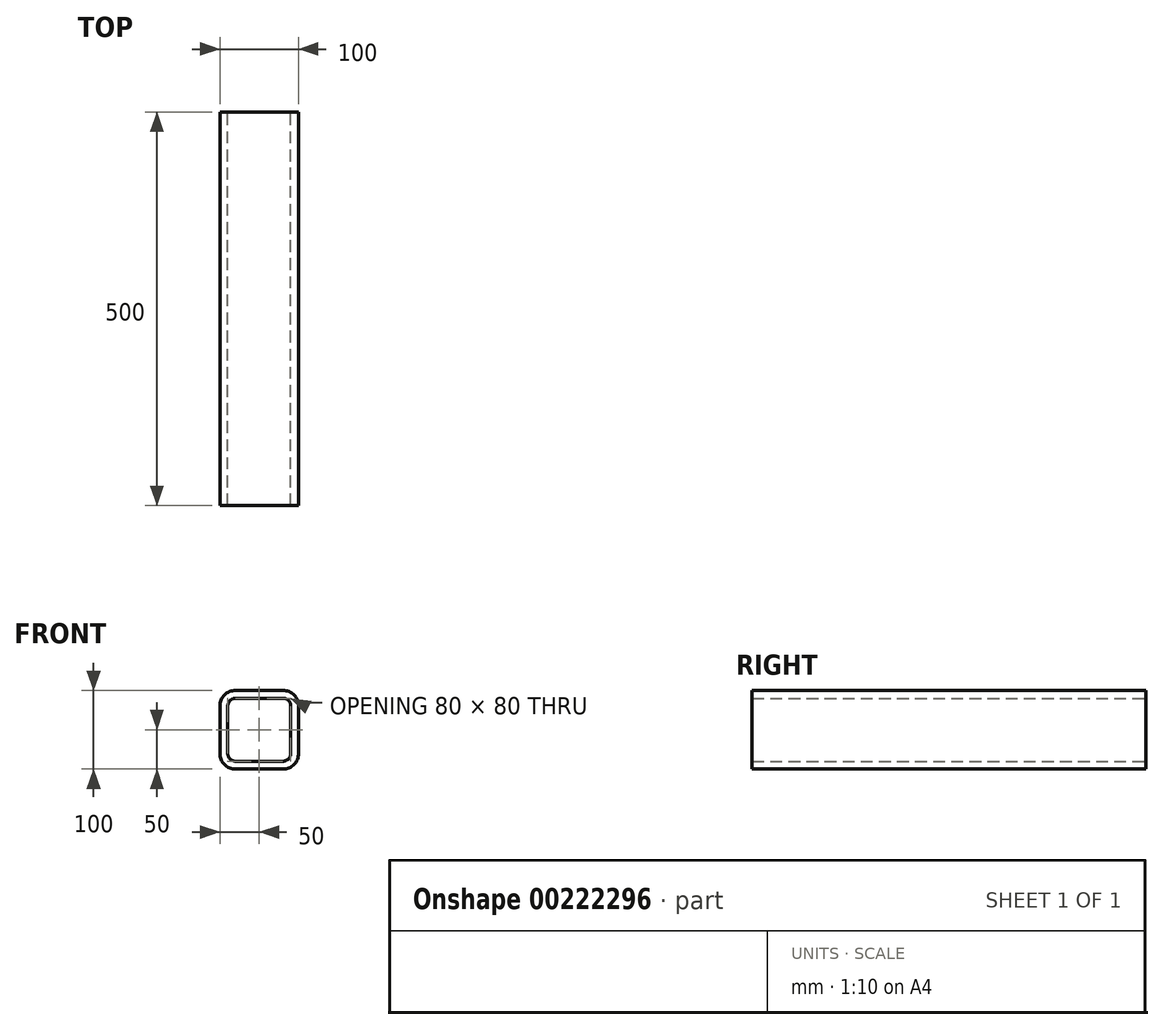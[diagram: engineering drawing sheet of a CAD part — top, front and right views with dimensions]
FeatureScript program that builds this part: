
annotation { "Feature Type Name" : "Feature", "Feature Type Description" : "" }
export const myFeature = defineFeature(function(context is Context, id is Id, definition is map)
    precondition{}
    {
        {
            var Q0;
            Q0=qCreatedBy(makeId("Front.planeOp"),FACE);
            var sketch = newSketch(context, id + "F0", { "sketchPlane" : qUnion([Q0])});
            skLineSegment(sketch, "E0.bottom", {"start": v(30, 50) * mm, "end": v(-30, 50) * mm});
            skLineSegment(sketch, "E0.top", {"start": v(30, -50) * mm, "end": v(-30, -50) * mm});
            skLineSegment(sketch, "E0.left", {"start": v(50, 30) * mm, "end": v(50, -30) * mm});
            skLineSegment(sketch, "E0.right", {"start": v(-50, 30) * mm, "end": v(-50, -30) * mm});
            skPoint(sketch, "E0.middle", {"position": v(0, 0) * mm});
            skPoint(sketch, "E1.visualSharp", {"position": v(-50, 50) * mm});
            skArc(sketch, "E1.filletArc", {"start": v(-30, 50) * mm, "mid": v(-44.14, 44.14) * mm, "end": v(-50, 30) * mm});
            skPoint(sketch, "E2.visualSharp", {"position": v(50, 50) * mm});
            skArc(sketch, "E2.filletArc", {"start": v(50, 30) * mm, "mid": v(44.14, 44.14) * mm, "end": v(30, 50) * mm});
            skPoint(sketch, "E3.visualSharp", {"position": v(50, -50) * mm});
            skArc(sketch, "E3.filletArc", {"start": v(30, -50) * mm, "mid": v(44.14, -44.14) * mm, "end": v(50, -30) * mm});
            skPoint(sketch, "E4.visualSharp", {"position": v(-50, -50) * mm});
            skArc(sketch, "E4.filletArc", {"start": v(-50, -30) * mm, "mid": v(-44.14, -44.14) * mm, "end": v(-30, -50) * mm});
            skLineSegment(sketch, "E5.0", {"start": v(-40, 30) * mm, "end": v(-40, -30) * mm});
            skArc(sketch, "E5.1", {"start": v(-30, 40) * mm, "mid": v(-37.07, 37.07) * mm, "end": v(-40, 30) * mm});
            skArc(sketch, "E5.2", {"start": v(-40, -30) * mm, "mid": v(-37.07, -37.07) * mm, "end": v(-30, -40) * mm});
            skLineSegment(sketch, "E5.3", {"start": v(30, 40) * mm, "end": v(-30, 40) * mm});
            skLineSegment(sketch, "E5.4", {"start": v(30, -40) * mm, "end": v(-30, -40) * mm});
            skArc(sketch, "E5.5", {"start": v(30, -40) * mm, "mid": v(37.07, -37.07) * mm, "end": v(40, -30) * mm});
            skLineSegment(sketch, "E5.6", {"start": v(40, 30) * mm, "end": v(40, -30) * mm});
            skArc(sketch, "E5.7", {"start": v(40, 30) * mm, "mid": v(37.07, 37.07) * mm, "end": v(30, 40) * mm});
            skSolve(sketch);
        }
        {
            var Q0;
            Q0=makeQuery(id+"F0.imprint","IMPRINT",FACE,{"disambiguationData":[TD([[makeQuery(id+"F0.imprint","IMPRINT",EDGE,{"derivedFrom":sQuery(id+"F0.wireOp",EDGE,"E0.bottom")}),1.0]])]});
            extrude(context, id + "F1", {"entities" : qUnion([Q0]), "depth" : 500 * mm, "offsetDistance" : 25 * mm, "symmetric" : true});
        }
    });
